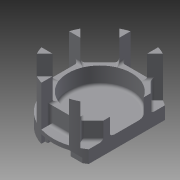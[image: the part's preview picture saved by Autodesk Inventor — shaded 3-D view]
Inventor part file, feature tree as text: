
AUTODESK INVENTOR PART (.ipt)
format: ipt  version: 2015 (Build 190159000, 159)  size: 356,864 bytes
history: native  units: in
note: dims shown in document units (in); Inventor stores cm internally (conversion verified against a paired STEP export)
features: extrude x4, sketch x3, fillet x3, chamfer x2
ambient origin geometry x8: Origin, YZ Plane, XZ Plane, XY Plane, X Axis, Y Axis, Z Axis, Center Point
bodies: Body1 (feature_tree)
feature tree (12):
  sketch  "Sketch7"  dims[d66=0.1181in d67=0.315in]
  sketch  "Sketch8"  dims[d69=135.0deg d70=0.8661in]
  sketch  "Sketch9"  dims[d71=0.0295in d72=0.0295in d73=0.0295in d74=0.0295in d75=0.0295in d76=0.0295in d77=0.0295in d78=0.0295in d79=0.0295in d80=0.0295in d81=0.0295in d82=0.0295in d83=0.0295in d84=0.0295in d85=0.0295in d86=0.0295in d87=0.7874in d88=1.1811in d89=1.1811in d90=0.3346in d91=0.3346in d92=0.0787in d97=0.1181in d98=0.0in d99=0.6299in d100=0.0in d101=1.2992in d102=0.0in d103=0.252in d104=0.0in d105=0.1181in d106=0.0787in d107=45.0deg d108=0.0591in d109=0.0787in d110=45.0deg d111=0.0787in d112=0.0787in d113=0.0787in]
  extrude  "Extrusion9"  Depth=0.315in
  extrude  "Extrusion10"  Depth=0.8661in
  extrude  "Extrusion11"  Depth=0.0787in
  extrude  "Extrusion12"  Depth=0.0787in
  chamfer  "Chamfer4"  Distance=0.0295in
  chamfer  "Chamfer5"  Distance=0.0295in
  fillet  "Fillet4"  Radius=0.0295in
  fillet  "Fillet5"  Radius=0.0295in
  fillet  "Fillet6"  Radius=0.0295in
